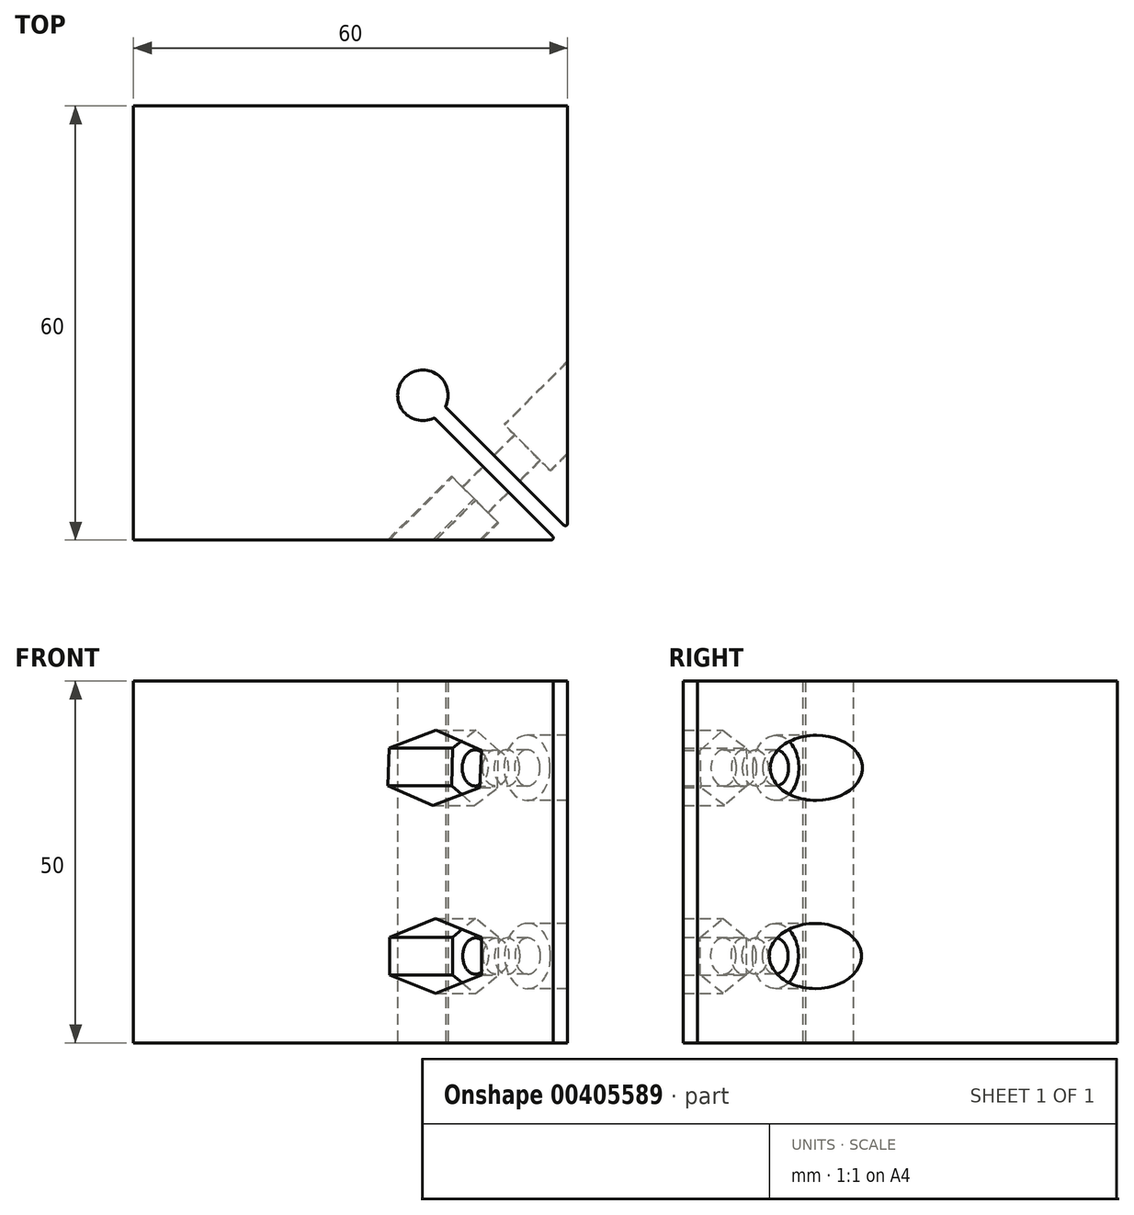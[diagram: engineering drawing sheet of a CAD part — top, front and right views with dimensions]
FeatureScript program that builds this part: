
annotation { "Feature Type Name" : "Feature", "Feature Type Description" : "" }
export const myFeature = defineFeature(function(context is Context, id is Id, definition is map)
    precondition{}
    {
        {
            var Q0;
            Q0=qCreatedBy(makeId("Top.planeOp"),FACE);
            var sketch = newSketch(context, id + "F0", { "sketchPlane" : qUnion([Q0])});
            skLineSegment(sketch, "E0.bottom", {"start": v(-61.79, 60.93) * mm, "end": v(-1.79, 60.93) * mm});
            skLineSegment(sketch, "E0.top", {"start": v(-61.79, 0.93) * mm, "end": v(-4.07, 0.93) * mm});
            skLineSegment(sketch, "E0.left", {"start": v(-61.79, 60.93) * mm, "end": v(-61.79, 0.93) * mm});
            skLineSegment(sketch, "E0.right", {"start": v(-1.79, 60.93) * mm, "end": v(-1.79, 3.21) * mm});
            skArc(sketch, "E1", {"start": v(-18.64, 19.43) * mm, "mid": v(-24.25, 23.4) * mm, "end": v(-20.29, 17.78) * mm});
            skLineSegment(sketch, "E2", {"start": v(-18.62, 19.32) * mm, "end": v(-2.3, 3) * mm});
            skLineSegment(sketch, "E3.MirrorCS", {"start": v(-20.17, 17.76) * mm, "end": v(-3.85, 1.44) * mm});
            skPoint(sketch, "E4.visualSharp", {"position": v(-20.22, 17.81) * mm});
            skArc(sketch, "E4.filletArc", {"start": v(-20.17, 17.76) * mm, "mid": v(-20.23, 17.8) * mm, "end": v(-20.29, 17.78) * mm});
            skPoint(sketch, "E5.visualSharp", {"position": v(-18.67, 19.37) * mm});
            skArc(sketch, "E5.filletArc", {"start": v(-18.64, 19.43) * mm, "mid": v(-18.64, 19.37) * mm, "end": v(-18.62, 19.32) * mm});
            skPoint(sketch, "E6.visualSharp", {"position": v(-1.79, 2.49) * mm});
            skArc(sketch, "E6.filletArc", {"start": v(-2.3, 3) * mm, "mid": v(-1.97, 2.94) * mm, "end": v(-1.79, 3.21) * mm});
            skPoint(sketch, "E7.visualSharp", {"position": v(-3.34, 0.93) * mm});
            skArc(sketch, "E7.filletArc", {"start": v(-4.07, 0.93) * mm, "mid": v(-3.79, 1.12) * mm, "end": v(-3.85, 1.44) * mm});
            skSolve(sketch);
        }
        {
            var Q0;
            Q0=qSketchRegion(id+"F0",true);
            extrude(context, id + "F1", {"entities" : qUnion([Q0]), "depth" : 50 * mm});
        }
        {
            var Q0;
            Q0=makeQuery(id+"F1.opExtrude","SWEPT_FACE",FACE,{"disambiguationData":[OSD([sQuery(id+"F0.wireOp",EDGE,"E2")])]});
            var sketch = newSketch(context, id + "F2", { "sketchPlane" : qUnion([Q0])});
            skCircle(sketch, "E8", {"center": v(-14.82, 12) * mm, "radius": 2.5 * mm});
            skCircle(sketch, "E9", {"center": v(-14.92, 38) * mm, "radius": 4.5 * mm});
            skCircle(sketch, "E10", {"center": v(-14.82, 12) * mm, "radius": 4.5 * mm});
            skCircle(sketch, "E11", {"center": v(-14.92, 38) * mm, "radius": 2.5 * mm});
            skCircle(sketch, "E12.cCircle", {"center": v(-14.92, 38) * mm, "radius": 4.5 * mm, "construction": true});
            skLineSegment(sketch, "E12.0", {"start": v(-10.5, 35.26) * mm, "end": v(-15.08, 32.8) * mm});
            skLineSegment(sketch, "E12.1", {"start": v(-15.08, 32.8) * mm, "end": v(-19.5, 35.54) * mm});
            skLineSegment(sketch, "E12.2", {"start": v(-19.5, 35.54) * mm, "end": v(-19.34, 40.74) * mm});
            skLineSegment(sketch, "E12.3", {"start": v(-19.34, 40.74) * mm, "end": v(-14.76, 43.2) * mm});
            skLineSegment(sketch, "E12.4", {"start": v(-14.76, 43.2) * mm, "end": v(-10.34, 40.46) * mm});
            skLineSegment(sketch, "E12.5", {"start": v(-10.34, 40.46) * mm, "end": v(-10.5, 35.26) * mm});
            skPoint(sketch, "E12.0.midPoint", {"position": v(-12.79, 34.04) * mm});
            skSolve(sketch);
        }
        {
            var Q0;
            Q0=sQuery(id+"F2.wireOp",VERTEX,"E9.center");
            var Q1;
            Q1=makeQuery(id+"F1.opExtrude","SWEPT_BODY",BODY,{"disambiguationData":[OSD([sQuery(id+"F0.wireOp",EDGE,"E0.bottom"),sQuery(id+"F0.wireOp",EDGE,"E0.top"),sQuery(id+"F0.wireOp",EDGE,"E0.left"),sQuery(id+"F0.wireOp",EDGE,"E0.right"),sQuery(id+"F0.wireOp",EDGE,"E1"),sQuery(id+"F0.wireOp",EDGE,"E2"),sQuery(id+"F0.wireOp",EDGE,"E3.MirrorCS"),sQuery(id+"F0.wireOp",EDGE,"E4.filletArc"),sQuery(id+"F0.wireOp",EDGE,"E5.filletArc"),sQuery(id+"F0.wireOp",EDGE,"E6.filletArc"),sQuery(id+"F0.wireOp",EDGE,"E7.filletArc")])]});
            hole(context, id + "F3", {"style" : HoleStyle.SIMPLE, "endStyle" : HoleEndStyle.THROUGH, "holeDiameter" : 5 * mm, "isTappedThrough" : true, "tappedDepth" : 12 * mm, "tapClearance" : 3, "locations" : qUnion([Q0]), "scope" : qUnion([Q1])});
        }
        {
            var Q0;
            Q0=sQuery(id+"F2.wireOp",VERTEX,"E9.center");
            var Q1;
            Q1=makeQuery(id+"F1.opExtrude","SWEPT_BODY",BODY,{"disambiguationData":[OSD([sQuery(id+"F0.wireOp",EDGE,"E0.bottom"),sQuery(id+"F0.wireOp",EDGE,"E0.top"),sQuery(id+"F0.wireOp",EDGE,"E0.left"),sQuery(id+"F0.wireOp",EDGE,"E0.right"),sQuery(id+"F0.wireOp",EDGE,"E1"),sQuery(id+"F0.wireOp",EDGE,"E2"),sQuery(id+"F0.wireOp",EDGE,"E3.MirrorCS"),sQuery(id+"F0.wireOp",EDGE,"E4.filletArc"),sQuery(id+"F0.wireOp",EDGE,"E5.filletArc"),sQuery(id+"F0.wireOp",EDGE,"E6.filletArc"),sQuery(id+"F0.wireOp",EDGE,"E7.filletArc")])]});
            hole(context, id + "F4", {"style" : HoleStyle.SIMPLE, "endStyle" : HoleEndStyle.THROUGH, "oppositeDirection" : true, "standardTappedOrClearance" : lookupTablePath({ "standard" : "自訂" }), "standardBlindInLast" : lookupTablePath({ "standard" : "自訂" }), "holeDiameter" : 5 * mm, "isTappedThrough" : true, "tappedDepth" : 12 * mm, "tapClearance" : 3, "locations" : qUnion([Q0]), "scope" : qUnion([Q1])});
        }
        {
            var Q0;
            Q0=makeQuery(id+"F2.imprint","IMPRINT",FACE,{"disambiguationData":[TD([[makeQuery(id+"F2.imprint","IMPRINT",EDGE,{"derivedFrom":sQuery(id+"F2.wireOp",EDGE,"E9")}),1.0]])]});
            var Q1;
            Q1=sQuery(id+"F2.wireOp",EDGE,"E9");
            extrude(context, id + "F5", {"entities" : qUnion([Q0]), "surfaceEntities" : qUnion([Q1]), "oppositeDirection" : true, "depth" : 25 * mm});
        }
        {
            var Q0;
            Q0=makeQuery(id+"F5.opExtrude","SWEPT_BODY",BODY,{"disambiguationData":[OSD([sQuery(id+"F2.wireOp",EDGE,"E9"),sQuery(id+"F2.wireOp",EDGE,"E11")])]});
            var Q1;
            Q1=makeQuery(id+"F1.opExtrude","SWEPT_BODY",BODY,{"disambiguationData":[OSD([sQuery(id+"F0.wireOp",EDGE,"E0.bottom"),sQuery(id+"F0.wireOp",EDGE,"E0.top"),sQuery(id+"F0.wireOp",EDGE,"E0.left"),sQuery(id+"F0.wireOp",EDGE,"E0.right"),sQuery(id+"F0.wireOp",EDGE,"E1"),sQuery(id+"F0.wireOp",EDGE,"E2"),sQuery(id+"F0.wireOp",EDGE,"E3.MirrorCS"),sQuery(id+"F0.wireOp",EDGE,"E4.filletArc"),sQuery(id+"F0.wireOp",EDGE,"E5.filletArc"),sQuery(id+"F0.wireOp",EDGE,"E6.filletArc"),sQuery(id+"F0.wireOp",EDGE,"E7.filletArc")])]});
            booleanBodies(context, id + "F6", {"operationType" : BooleanOperationType.SUBTRACTION, "tools" : qUnion([Q0]), "targets" : qUnion([Q1])});
        }
        {
            var Q0;
            Q0=makeQuery(id+"F2.imprint","IMPRINT",FACE,{"disambiguationData":[TD([[makeQuery(id+"F2.imprint","IMPRINT",EDGE,{"derivedFrom":sQuery(id+"F2.wireOp",EDGE,"E9")}),1.0]])]});
            extrude(context, id + "F7", {"entities" : qUnion([Q0]), "operationType" : NewBodyOperationType.ADD, "oppositeDirection" : true, "depth" : 4 * mm});
        }
        {
            var Q0;
            Q0=sQuery(id+"F2.wireOp",VERTEX,"E8.center");
            var Q1;
            Q1=makeQuery(id+"F1.opExtrude","SWEPT_BODY",BODY,{"disambiguationData":[OSD([sQuery(id+"F0.wireOp",EDGE,"E0.bottom"),sQuery(id+"F0.wireOp",EDGE,"E0.top"),sQuery(id+"F0.wireOp",EDGE,"E0.left"),sQuery(id+"F0.wireOp",EDGE,"E0.right"),sQuery(id+"F0.wireOp",EDGE,"E1"),sQuery(id+"F0.wireOp",EDGE,"E2"),sQuery(id+"F0.wireOp",EDGE,"E3.MirrorCS"),sQuery(id+"F0.wireOp",EDGE,"E4.filletArc"),sQuery(id+"F0.wireOp",EDGE,"E5.filletArc"),sQuery(id+"F0.wireOp",EDGE,"E6.filletArc"),sQuery(id+"F0.wireOp",EDGE,"E7.filletArc")])]});
            hole(context, id + "F8", {"style" : HoleStyle.SIMPLE, "endStyle" : HoleEndStyle.THROUGH, "oppositeDirection" : true, "standardTappedOrClearance" : lookupTablePath({ "standard" : "自訂" }), "standardBlindInLast" : lookupTablePath({ "standard" : "自訂" }), "holeDiameter" : 5 * mm, "isTappedThrough" : true, "tappedDepth" : 12 * mm, "tapClearance" : 3, "locations" : qUnion([Q0]), "scope" : qUnion([Q1])});
        }
        {
            var Q0;
            Q0=makeQuery(id+"F1.opExtrude","SWEPT_FACE",FACE,{"disambiguationData":[OSD([sQuery(id+"F0.wireOp",EDGE,"E3.MirrorCS")])]});
            var sketch = newSketch(context, id + "F9", { "sketchPlane" : qUnion([Q0])});
            skCircle(sketch, "E13.cCircle", {"center": v(14.92, 38) * mm, "radius": 4.5 * mm, "construction": true});
            skLineSegment(sketch, "E13.0", {"start": v(10.34, 40.45) * mm, "end": v(14.75, 43.2) * mm});
            skLineSegment(sketch, "E13.1", {"start": v(14.75, 43.2) * mm, "end": v(19.33, 40.74) * mm});
            skLineSegment(sketch, "E13.2", {"start": v(19.33, 40.74) * mm, "end": v(19.5, 35.55) * mm});
            skLineSegment(sketch, "E13.3", {"start": v(19.5, 35.55) * mm, "end": v(15.08, 32.8) * mm});
            skLineSegment(sketch, "E13.4", {"start": v(15.08, 32.8) * mm, "end": v(10.5, 35.26) * mm});
            skLineSegment(sketch, "E13.5", {"start": v(10.5, 35.26) * mm, "end": v(10.34, 40.45) * mm});
            skPoint(sketch, "E13.0.midPoint", {"position": v(12.54, 41.82) * mm});
            skCircle(sketch, "E14", {"center": v(14.92, 38) * mm, "radius": 2.5 * mm});
            skCircle(sketch, "E15.cCircle", {"center": v(14.82, 12) * mm, "radius": 4.5 * mm, "construction": true});
            skLineSegment(sketch, "E15.0", {"start": v(19.32, 14.6) * mm, "end": v(19.32, 9.4) * mm});
            skLineSegment(sketch, "E15.1", {"start": v(19.32, 9.4) * mm, "end": v(14.82, 6.8) * mm});
            skLineSegment(sketch, "E15.2", {"start": v(14.82, 6.8) * mm, "end": v(10.32, 9.4) * mm});
            skLineSegment(sketch, "E15.3", {"start": v(10.32, 9.4) * mm, "end": v(10.32, 14.6) * mm});
            skLineSegment(sketch, "E15.4", {"start": v(10.32, 14.6) * mm, "end": v(14.82, 17.2) * mm});
            skLineSegment(sketch, "E15.5", {"start": v(14.82, 17.2) * mm, "end": v(19.32, 14.6) * mm});
            skPoint(sketch, "E15.0.midPoint", {"position": v(19.32, 12) * mm});
            skSolve(sketch);
        }
        {
            var Q0;
            Q0=qSketchRegion(id+"F9",true);
            extrude(context, id + "F10", {"entities" : qUnion([Q0]), "operationType" : NewBodyOperationType.REMOVE, "oppositeDirection" : true, "depth" : 25 * mm});
        }
        {
            var Q0;
            Q0=makeQuery(id+"F9.imprint","IMPRINT",FACE,{"disambiguationData":[TD([[makeQuery(id+"F9.imprint","IMPRINT",EDGE,{"derivedFrom":sQuery(id+"F9.wireOp",EDGE,"E13.0")}),-1.0]])]});
            var Q1;
            Q1=sQuery(id+"F9.wireOp",EDGE,"E13.2");
            extrude(context, id + "F11", {"entities" : qUnion([Q0]), "operationType" : NewBodyOperationType.ADD, "surfaceEntities" : qUnion([Q1]), "oppositeDirection" : true, "depth" : 4 * mm});
        }
        {
            var Q0;
            Q0=sQuery(id+"F2.wireOp",VERTEX,"E8.center");
            var Q1;
            Q1=makeQuery(id+"F1.opExtrude","SWEPT_BODY",BODY,{"disambiguationData":[OSD([sQuery(id+"F0.wireOp",EDGE,"E0.bottom"),sQuery(id+"F0.wireOp",EDGE,"E0.top"),sQuery(id+"F0.wireOp",EDGE,"E0.left"),sQuery(id+"F0.wireOp",EDGE,"E0.right"),sQuery(id+"F0.wireOp",EDGE,"E1"),sQuery(id+"F0.wireOp",EDGE,"E2"),sQuery(id+"F0.wireOp",EDGE,"E3.MirrorCS"),sQuery(id+"F0.wireOp",EDGE,"E4.filletArc"),sQuery(id+"F0.wireOp",EDGE,"E5.filletArc"),sQuery(id+"F0.wireOp",EDGE,"E6.filletArc"),sQuery(id+"F0.wireOp",EDGE,"E7.filletArc")])]});
            hole(context, id + "F12", {"style" : HoleStyle.SIMPLE, "endStyle" : HoleEndStyle.THROUGH, "standardTappedOrClearance" : lookupTablePath({ "standard" : "自訂" }), "standardBlindInLast" : lookupTablePath({ "standard" : "自訂" }), "holeDiameter" : 9 * mm, "isTappedThrough" : true, "tappedDepth" : 12 * mm, "tapClearance" : 3, "locations" : qUnion([Q0]), "scope" : qUnion([Q1])});
        }
        {
            var Q0;
            Q0=makeQuery(id+"F2.imprint","IMPRINT",FACE,{"disambiguationData":[TD([[makeQuery(id+"F2.imprint","IMPRINT",EDGE,{"derivedFrom":sQuery(id+"F2.wireOp",EDGE,"E8")}),-1.0]])]});
            extrude(context, id + "F13", {"entities" : qUnion([Q0]), "operationType" : NewBodyOperationType.ADD, "oppositeDirection" : true, "depth" : 4 * mm});
        }
        {
            var Q0;
            Q0=makeQuery(id+"F9.imprint","IMPRINT",FACE,{"disambiguationData":[TD([[makeQuery(id+"F9.imprint","IMPRINT",EDGE,{"derivedFrom":sQuery(id+"F9.wireOp",EDGE,"E15.0")}),-1.0]])]});
            extrude(context, id + "F14", {"entities" : qUnion([Q0]), "operationType" : NewBodyOperationType.ADD, "oppositeDirection" : true, "depth" : 4 * mm});
        }
    });
